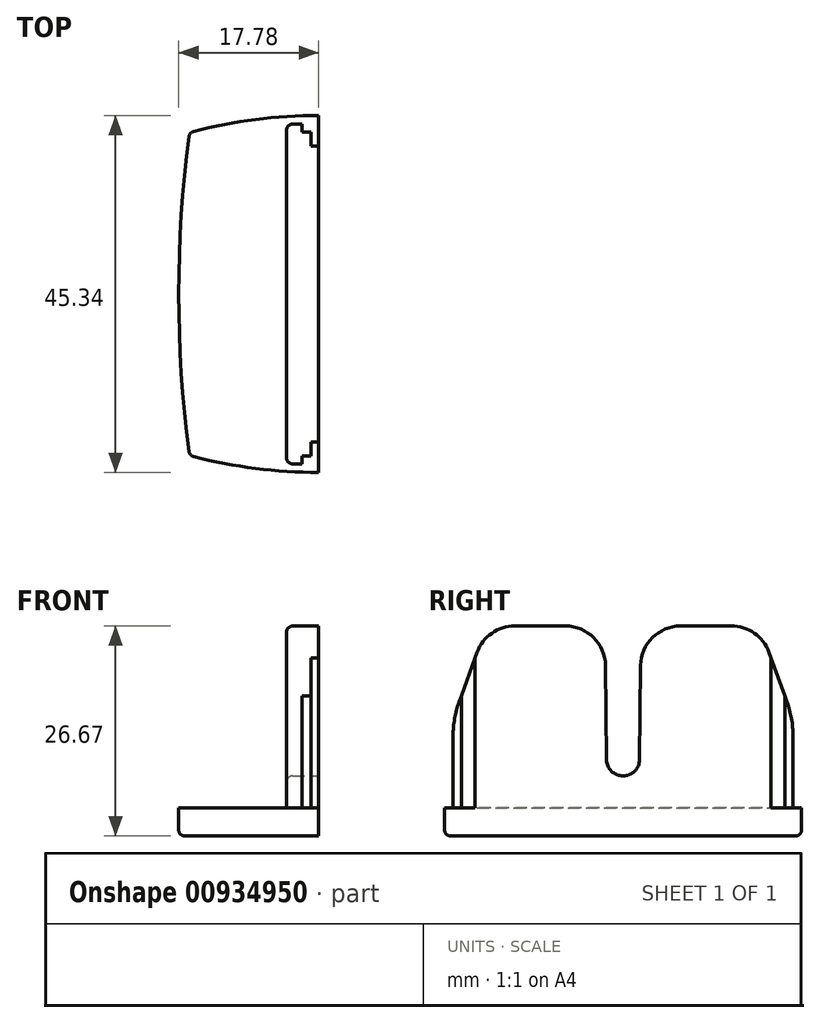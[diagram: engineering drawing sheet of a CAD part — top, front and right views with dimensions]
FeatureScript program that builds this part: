
annotation { "Feature Type Name" : "Feature", "Feature Type Description" : "" }
export const myFeature = defineFeature(function(context is Context, id is Id, definition is map)
    precondition{}
    {
        {
            var Q0;
            Q0=qCreatedBy(makeId("Front.planeOp"),FACE);
            var sketch = newSketch(context, id + "F0", { "sketchPlane" : qUnion([Q0])});
            skLineSegment(sketch, "E0", {"start": v(-17.78, 0) * mm, "end": v(0, 0) * mm});
            skLineSegment(sketch, "E1", {"start": v(0, 0) * mm, "end": v(0, 26.67) * mm});
            skLineSegment(sketch, "E2", {"start": v(0, 26.67) * mm, "end": v(-4.06, 26.67) * mm});
            skLineSegment(sketch, "E3", {"start": v(-4.06, 26.67) * mm, "end": v(-4.06, 3.56) * mm});
            skLineSegment(sketch, "E4", {"start": v(-4.06, 3.56) * mm, "end": v(-17.78, 3.56) * mm});
            skLineSegment(sketch, "E5", {"start": v(-17.78, 3.56) * mm, "end": v(-17.78, 0) * mm});
            skSolve(sketch);
        }
        {
            var Q0;
            Q0 = qSketchRegion(id + "F0", true);
            extrude(context, id + "F1", {"entities" : qUnion([Q0]), "depth" : 22.67 * mm, "offsetDistance" : 25.4 * mm, "hasSecondDirection" : true, "secondDirectionOppositeDirection" : true, "secondDirectionDepth" : 22.67 * mm});
        }
        {
            var Q0;
            Q0=makeQuery(id+"F1.opExtrude","SWEPT_FACE",FACE,{"disambiguationData":[OSD([sQuery(id+"F0.wireOp",EDGE,"E1")])]});
            var sketch = newSketch(context, id + "F2", { "sketchPlane" : qUnion([Q0])});
            skLineSegment(sketch, "E6", {"start": v(22.67, 3.56) * mm, "end": v(21.59, 3.56) * mm});
            skLineSegment(sketch, "E7", {"start": v(21.59, 3.56) * mm, "end": v(21.59, 12.7) * mm});
            skArc(sketch, "E8", {"start": v(21.6, 12.7) * mm, "mid": v(21.4, 14.9) * mm, "end": v(20.82, 17.04) * mm});
            skLineSegment(sketch, "E9", {"start": v(20.82, 17.04) * mm, "end": v(18.54, 23.33) * mm});
            skArc(sketch, "E10", {"start": v(18.54, 23.33) * mm, "mid": v(16.68, 25.75) * mm, "end": v(13.76, 26.67) * mm});
            skArc(sketch, "E11", {"start": v(7.31, 26.67) * mm, "mid": v(3.74, 25.2) * mm, "end": v(2.24, 21.65) * mm});
            skArc(sketch, "E12", {"start": v(0, 7.62) * mm, "mid": v(1.47, 8.23) * mm, "end": v(2.1, 9.7) * mm});
            skLineSegment(sketch, "E13", {"start": v(13.76, 26.67) * mm, "end": v(7.31, 26.67) * mm});
            skLineSegment(sketch, "E14", {"start": v(2.24, 21.65) * mm, "end": v(2.1, 9.7) * mm});
            skLineSegment(sketch, "E15", {"start": v(22.67, 3.56) * mm, "end": v(22.67, 27.94) * mm});
            skLineSegment(sketch, "E16", {"start": v(22.67, 27.94) * mm, "end": v(0, 27.94) * mm});
            skLineSegment(sketch, "E17.MirrorCS", {"start": v(-20.82, 17.04) * mm, "end": v(-18.54, 23.33) * mm});
            skLineSegment(sketch, "E18.MirrorCS", {"start": v(-22.67, 27.94) * mm, "end": v(0, 27.94) * mm});
            skLineSegment(sketch, "E19.MirrorCS", {"start": v(-22.67, 3.56) * mm, "end": v(-21.59, 3.56) * mm});
            skArc(sketch, "E20.MirrorCS", {"start": v(0, 7.62) * mm, "mid": v(-1.47, 8.23) * mm, "end": v(-2.1, 9.7) * mm});
            skLineSegment(sketch, "E21.MirrorCS", {"start": v(-21.59, 3.56) * mm, "end": v(-21.59, 12.7) * mm});
            skArc(sketch, "E22.MirrorCS", {"start": v(-18.54, 23.33) * mm, "mid": v(-16.68, 25.75) * mm, "end": v(-13.76, 26.67) * mm});
            skLineSegment(sketch, "E23.MirrorCS", {"start": v(-2.24, 21.65) * mm, "end": v(-2.1, 9.7) * mm});
            skArc(sketch, "E24.MirrorCS", {"start": v(-21.6, 12.7) * mm, "mid": v(-21.4, 14.9) * mm, "end": v(-20.82, 17.04) * mm});
            skLineSegment(sketch, "E25.MirrorCS", {"start": v(-13.76, 26.67) * mm, "end": v(-7.31, 26.67) * mm});
            skArc(sketch, "E26.MirrorCS", {"start": v(-7.31, 26.67) * mm, "mid": v(-3.74, 25.2) * mm, "end": v(-2.24, 21.65) * mm});
            skLineSegment(sketch, "E27.MirrorCS", {"start": v(-22.67, 3.56) * mm, "end": v(-22.67, 27.94) * mm});
            skSolve(sketch);
        }
        {
            var Q0;
            Q0 = qSketchRegion(id + "F2", true);
            extrude(context, id + "F3", {"entities" : qUnion([Q0]), "operationType" : NewBodyOperationType.REMOVE, "oppositeDirection" : true, "depth" : 25.4 * mm, "offsetDistance" : 25.4 * mm});
        }
        {
            var Q0;
            Q0=makeQuery(id+"F3.boolean.opBoolean","MERGE",FACE,{"derivedFrom":[makeQuery(id+"F1.opExtrude","SWEPT_FACE",FACE,{"disambiguationData":[OSD([sQuery(id+"F0.wireOp",EDGE,"E4")])]})],"fromTools":[makeQuery(id+"F3.opExtrude","SWEPT_FACE",FACE,{"disambiguationData":[OSD([sQuery(id+"F2.wireOp",EDGE,"E6")])]}),makeQuery(id+"F3.opExtrude","SWEPT_FACE",FACE,{"disambiguationData":[OSD([sQuery(id+"F2.wireOp",EDGE,"E19.MirrorCS")])]})]});
            var sketch = newSketch(context, id + "F4", { "sketchPlane" : qUnion([Q0])});
            skLineSegment(sketch, "E28", {"start": v(-2.13, 22.67) * mm, "end": v(-2.13, 20.55) * mm});
            skLineSegment(sketch, "E29", {"start": v(-2.13, 20.55) * mm, "end": v(-0.97, 20.55) * mm});
            skLineSegment(sketch, "E30", {"start": v(-0.97, 20.55) * mm, "end": v(-0.97, 18.8) * mm});
            skLineSegment(sketch, "E31", {"start": v(-0.97, 18.8) * mm, "end": v(0, 18.8) * mm});
            skLineSegment(sketch, "E32", {"start": v(0, 18.8) * mm, "end": v(0, 22.67) * mm});
            skLineSegment(sketch, "E33", {"start": v(0, 22.67) * mm, "end": v(-2.13, 22.67) * mm});
            skLineSegment(sketch, "E34.MirrorCS", {"start": v(-2.13, -22.67) * mm, "end": v(-2.13, -20.55) * mm});
            skLineSegment(sketch, "E35.MirrorCS", {"start": v(-0.97, -20.55) * mm, "end": v(-0.97, -18.8) * mm});
            skLineSegment(sketch, "E36.MirrorCS", {"start": v(-0.97, -18.8) * mm, "end": v(0, -18.8) * mm});
            skLineSegment(sketch, "E37.MirrorCS", {"start": v(-2.13, -20.55) * mm, "end": v(-0.97, -20.55) * mm});
            skLineSegment(sketch, "E38.MirrorCS", {"start": v(0, -18.8) * mm, "end": v(0, -22.67) * mm});
            skLineSegment(sketch, "E39.MirrorCS", {"start": v(0, -22.67) * mm, "end": v(-2.13, -22.67) * mm});
            skSolve(sketch);
        }
        {
            var Q0;
            Q0 = qSketchRegion(id + "F4", true);
            extrude(context, id + "F5", {"entities" : qUnion([Q0]), "operationType" : NewBodyOperationType.REMOVE, "depth" : 25.4 * mm, "offsetDistance" : 25.4 * mm});
        }
        {
            var Q0;
            Q0=makeQuery(id+"F5.boolean.opBoolean","MERGE",FACE,{"derivedFrom":[makeQuery(id+"F3.boolean.opBoolean","MERGE",FACE,{"derivedFrom":[makeQuery(id+"F1.opExtrude","SWEPT_FACE",FACE,{"disambiguationData":[OSD([sQuery(id+"F0.wireOp",EDGE,"E4")])]})],"fromTools":[makeQuery(id+"F3.opExtrude","SWEPT_FACE",FACE,{"disambiguationData":[OSD([sQuery(id+"F2.wireOp",EDGE,"E6")])]}),makeQuery(id+"F3.opExtrude","SWEPT_FACE",FACE,{"disambiguationData":[OSD([sQuery(id+"F2.wireOp",EDGE,"E19.MirrorCS")])]})]})],"fromTools":[makeQuery(id+"F5.opExtrude","CAP_FACE",FACE,{"disambiguationData":[OSD([sQuery(id+"F4.wireOp",EDGE,"E28"),sQuery(id+"F4.wireOp",EDGE,"E29"),sQuery(id+"F4.wireOp",EDGE,"E30"),sQuery(id+"F4.wireOp",EDGE,"E31"),sQuery(id+"F4.wireOp",EDGE,"E32"),sQuery(id+"F4.wireOp",EDGE,"E33")])],"isStart":true}),makeQuery(id+"F5.opExtrude","CAP_FACE",FACE,{"disambiguationData":[OSD([sQuery(id+"F4.wireOp",EDGE,"E34.MirrorCS"),sQuery(id+"F4.wireOp",EDGE,"E35.MirrorCS"),sQuery(id+"F4.wireOp",EDGE,"E36.MirrorCS"),sQuery(id+"F4.wireOp",EDGE,"E37.MirrorCS"),sQuery(id+"F4.wireOp",EDGE,"E38.MirrorCS"),sQuery(id+"F4.wireOp",EDGE,"E39.MirrorCS")])],"isStart":true})]});
            var sketch = newSketch(context, id + "F6", { "sketchPlane" : qUnion([Q0])});
            skArc(sketch, "E40", {"start": v(0, 22.67) * mm, "mid": v(-8.27, 22.13) * mm, "end": v(-16.4, 20.52) * mm});
            skArc(sketch, "E41", {"start": v(-16.4, 20.52) * mm, "mid": v(-17.78, 0) * mm, "end": v(-16.4, -20.52) * mm});
            skArc(sketch, "E42", {"start": v(-16.4, -20.52) * mm, "mid": v(-8.27, -22.13) * mm, "end": v(0, -22.67) * mm});
            skLineSegment(sketch, "E43", {"start": v(0, 22.67) * mm, "end": v(0, 25.4) * mm});
            skLineSegment(sketch, "E44", {"start": v(0, 25.4) * mm, "end": v(-25.4, 25.4) * mm});
            skLineSegment(sketch, "E45", {"start": v(-25.4, 25.4) * mm, "end": v(-25.4, -25.4) * mm});
            skLineSegment(sketch, "E46", {"start": v(-25.4, -25.4) * mm, "end": v(0, -25.4) * mm});
            skLineSegment(sketch, "E47", {"start": v(0, -25.4) * mm, "end": v(0, -22.67) * mm});
            skSolve(sketch);
        }
        {
            var Q0;
            Q0 = qSketchRegion(id + "F6", true);
            extrude(context, id + "F7", {"entities" : qUnion([Q0]), "operationType" : NewBodyOperationType.REMOVE, "oppositeDirection" : true, "depth" : 25.4 * mm, "offsetDistance" : 25.4 * mm});
        }
        {
            var Q0;
            Q0=makeQuery(id+"F7.boolean.opBoolean","INTERSECT",EDGE,{"derivedFrom":[makeQuery(id+"F1.opExtrude","SWEPT_FACE",FACE,{"disambiguationData":[OSD([sQuery(id+"F0.wireOp",EDGE,"E0")])]}),makeQuery(id+"F7.opExtrude","SWEPT_FACE",FACE,{"disambiguationData":[OSD([sQuery(id+"F6.wireOp",EDGE,"E42")])]})]});
            var Q1;
            Q1=makeQuery(id+"F7.boolean.opBoolean","INTERSECT",EDGE,{"derivedFrom":[makeQuery(id+"F1.opExtrude","SWEPT_FACE",FACE,{"disambiguationData":[OSD([sQuery(id+"F0.wireOp",EDGE,"E0")])]}),makeQuery(id+"F7.opExtrude","SWEPT_FACE",FACE,{"disambiguationData":[OSD([sQuery(id+"F6.wireOp",EDGE,"E41")])]})]});
            var Q2;
            Q2=makeQuery(id+"F7.boolean.opBoolean","INTERSECT",EDGE,{"derivedFrom":[makeQuery(id+"F1.opExtrude","SWEPT_FACE",FACE,{"disambiguationData":[OSD([sQuery(id+"F0.wireOp",EDGE,"E0")])]}),makeQuery(id+"F7.opExtrude","SWEPT_FACE",FACE,{"disambiguationData":[OSD([sQuery(id+"F6.wireOp",EDGE,"E40")])]})]});
            var Q3;
            Q3=makeQuery(id+"F7.boolean.opBoolean","COPY",EDGE,{"derivedFrom":makeQuery(id+"F7.opExtrude","SWEPT_EDGE",EDGE,{"disambiguationData":[OSD([sQuery(id+"F6.wireOp",EDGE,"E41"),sQuery(id+"F6.wireOp",EDGE,"E42")])]})});
            var Q4;
            Q4=makeQuery(id+"F7.boolean.opBoolean","COPY",EDGE,{"derivedFrom":makeQuery(id+"F7.opExtrude","SWEPT_EDGE",EDGE,{"disambiguationData":[OSD([sQuery(id+"F6.wireOp",EDGE,"E40"),sQuery(id+"F6.wireOp",EDGE,"E41")])]})});
            var Q5;
            Q5=makeQuery(id+"F3.boolean.opBoolean","INTERSECT",EDGE,{"derivedFrom":[makeQuery(id+"F1.opExtrude","SWEPT_FACE",FACE,{"disambiguationData":[OSD([sQuery(id+"F0.wireOp",EDGE,"E3")])]}),makeQuery(id+"F3.opExtrude","SWEPT_FACE",FACE,{"disambiguationData":[OSD([sQuery(id+"F2.wireOp",EDGE,"E7")])]})]});
            var Q6;
            Q6=makeQuery(id+"F3.boolean.opBoolean","COPY",EDGE,{"derivedFrom":makeQuery(id+"F3.opExtrude","CAP_EDGE",EDGE,{"disambiguationData":[OSD([sQuery(id+"F2.wireOp",EDGE,"E12"),sQuery(id+"F2.wireOp",EDGE,"E20.MirrorCS")])],"isStart":true})});
            fillet(context, id + "F8", {"entities" : qUnion([Q0, Q1, Q2, Q3, Q4, Q5, Q6]), "radius" : 0.76 * mm, "tangentPropagation" : true, "allowEdgeOverflow" : false});
        }
    });
